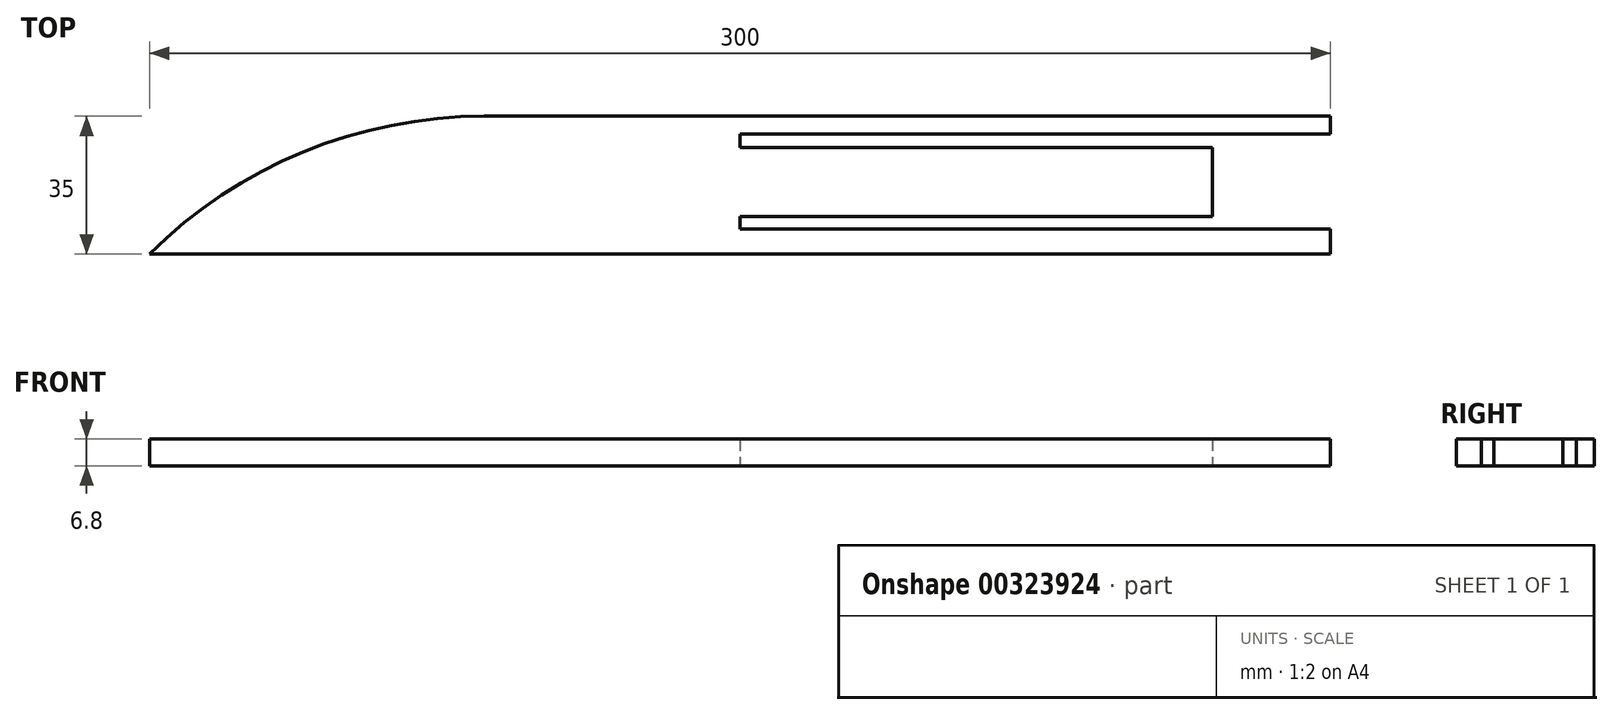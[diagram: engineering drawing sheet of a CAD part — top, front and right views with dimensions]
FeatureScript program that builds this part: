
annotation { "Feature Type Name" : "Feature", "Feature Type Description" : "" }
export const myFeature = defineFeature(function(context is Context, id is Id, definition is map)
    precondition{}
    {
        {
            var Q0;
            Q0=qCreatedBy(makeId("Top.planeOp"),FACE);
            var sketch = newSketch(context, id + "F0", { "sketchPlane" : qUnion([Q0])});
            skLineSegment(sketch, "E0.bottom", {"start": v(-150, 17.5) * mm, "end": v(150, 17.5) * mm});
            skLineSegment(sketch, "E0.top", {"start": v(-150, -17.5) * mm, "end": v(150, -17.5) * mm});
            skLineSegment(sketch, "E0.left", {"start": v(-150, 17.5) * mm, "end": v(-150, -17.5) * mm});
            skLineSegment(sketch, "E0.right", {"start": v(150, 17.5) * mm, "end": v(150, 12.91) * mm});
            skPoint(sketch, "E0.middle", {"position": v(0, 0) * mm});
            skLineSegment(sketch, "E1", {"start": v(0, 12.91) * mm, "end": v(150, 12.91) * mm});
            skLineSegment(sketch, "E2", {"start": v(0, 9.55) * mm, "end": v(150, 9.55) * mm});
            skLineSegment(sketch, "E3", {"start": v(0, 9.55) * mm, "end": v(0, 12.91) * mm});
            skLineSegment(sketch, "E4", {"start": v(0, -11.11) * mm, "end": v(150, -11.11) * mm});
            skLineSegment(sketch, "E5", {"start": v(150, -8.01) * mm, "end": v(0, -8.01) * mm});
            skLineSegment(sketch, "E6", {"start": v(0, -8.01) * mm, "end": v(0, -11.11) * mm});
            skLineSegment(sketch, "E7.trimOffspring", {"start": v(150, -11.11) * mm, "end": v(150, -17.5) * mm});
            skLineSegment(sketch, "E8.trimOffspring", {"start": v(150, 9.55) * mm, "end": v(150, -8.01) * mm});
            skSolve(sketch);
        }
        {
            var Q0;
            Q0=makeQuery(id+"F0.imprint","IMPRINT",FACE,{"disambiguationData":[TD([[makeQuery(id+"F0.imprint","IMPRINT",EDGE,{"derivedFrom":sQuery(id+"F0.wireOp",EDGE,"E0.bottom")}),-1.0]])]});
            extrude(context, id + "F1", {"entities" : qUnion([Q0]), "depth" : 6 * mm});
        }
        {
            var Q0;
            Q0=makeQuery(id+"F1.opExtrude","CAP_FACE",FACE,{"disambiguationData":[OSD([sQuery(id+"F0.wireOp",EDGE,"E0.bottom"),sQuery(id+"F0.wireOp",EDGE,"E0.top"),sQuery(id+"F0.wireOp",EDGE,"E0.left"),sQuery(id+"F0.wireOp",EDGE,"E0.right"),sQuery(id+"F0.wireOp",EDGE,"E1"),sQuery(id+"F0.wireOp",EDGE,"E2"),sQuery(id+"F0.wireOp",EDGE,"E3"),sQuery(id+"F0.wireOp",EDGE,"E4"),sQuery(id+"F0.wireOp",EDGE,"E5"),sQuery(id+"F0.wireOp",EDGE,"E6"),sQuery(id+"F0.wireOp",EDGE,"E7.trimOffspring"),sQuery(id+"F0.wireOp",EDGE,"E8.trimOffspring")])],"isStart":true});
            var Q1;
            Q1=makeQuery(id+"F1.opExtrude","CAP_FACE",FACE,{"disambiguationData":[OSD([sQuery(id+"F0.wireOp",EDGE,"E0.bottom"),sQuery(id+"F0.wireOp",EDGE,"E0.top"),sQuery(id+"F0.wireOp",EDGE,"E0.left"),sQuery(id+"F0.wireOp",EDGE,"E0.right"),sQuery(id+"F0.wireOp",EDGE,"E1"),sQuery(id+"F0.wireOp",EDGE,"E2"),sQuery(id+"F0.wireOp",EDGE,"E3"),sQuery(id+"F0.wireOp",EDGE,"E4"),sQuery(id+"F0.wireOp",EDGE,"E5"),sQuery(id+"F0.wireOp",EDGE,"E6"),sQuery(id+"F0.wireOp",EDGE,"E7.trimOffspring"),sQuery(id+"F0.wireOp",EDGE,"E8.trimOffspring")])],"isStart":false});
            extrude(context, id + "F2", {"entities" : qUnion([Q0, Q1]), "operationType" : NewBodyOperationType.ADD, "depth" : 0.8 * mm});
        }
        {
            var Q0;
            {var subQ0=sQuery(id+"F0.wireOp",EDGE,"E0.left");var subQ1=sQuery(id+"F0.wireOp",EDGE,"E0.bottom");Q0=makeQuery(id+"F2.boolean.opBoolean","MERGE",EDGE,{"derivedFrom":[makeQuery(id+"F1.opExtrude","SWEPT_EDGE",EDGE,{"disambiguationData":[OSD([subQ1,subQ0])]}),makeQuery(id+"F2.opExtrude","SWEPT_EDGE",EDGE,{"disambiguationData":[OSD([subQ1,subQ0]),TDD([makeQuery(id+"F1.opExtrude","CAP_VERTEX",VERTEX,{"disambiguationData":[OSD([subQ1,subQ0])],"isStart":true})])]})]});}
            fillet(context, id + "F3", {"entities" : qUnion([Q0]), "radius" : 120.7 * mm, "tangentPropagation" : true, "allowEdgeOverflow" : false});
        }
        {
            var Q0;
            {var subQ0=sQuery(id+"F0.wireOp",EDGE,"E8.trimOffspring");Q0=makeQuery(id+"F2.boolean.opBoolean","MERGE",FACE,{"derivedFrom":[makeQuery(id+"F1.opExtrude","SWEPT_FACE",FACE,{"disambiguationData":[OSD([subQ0])]}),makeQuery(id+"F2.opExtrude","SWEPT_FACE",FACE,{"disambiguationData":[OSD([subQ0]),TDD([makeQuery(id+"F1.opExtrude","CAP_EDGE",EDGE,{"disambiguationData":[OSD([subQ0])],"isStart":true})])]})]});}
            extrude(context, id + "F4", {"entities" : qUnion([Q0]), "operationType" : NewBodyOperationType.REMOVE, "oppositeDirection" : true, "depth" : 30 * mm});
        }
    });
